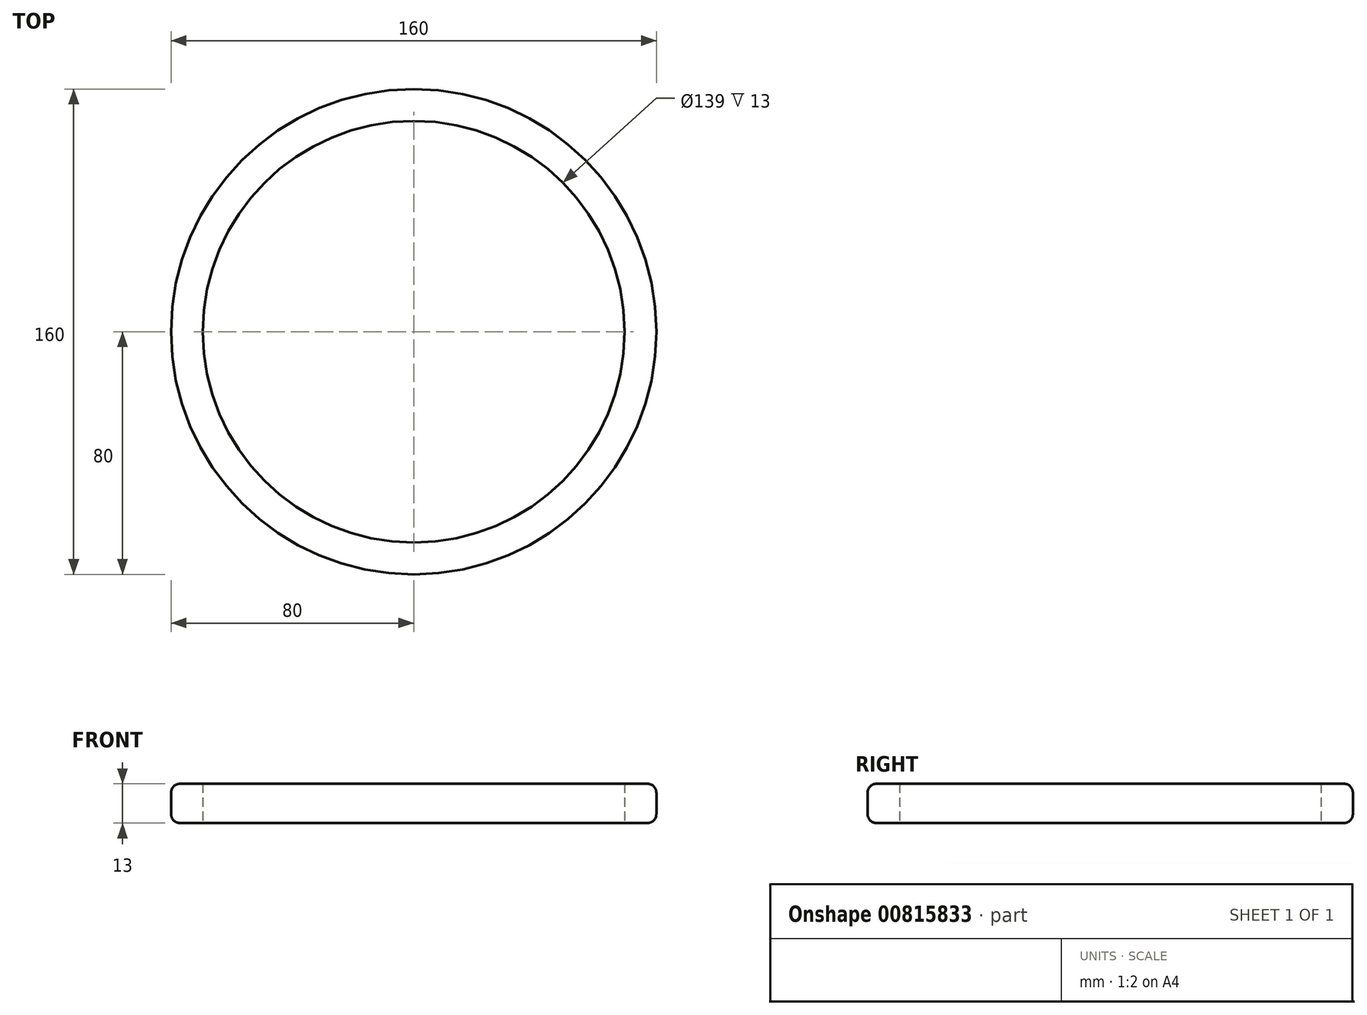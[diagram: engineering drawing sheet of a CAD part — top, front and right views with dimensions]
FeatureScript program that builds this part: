
annotation { "Feature Type Name" : "Feature", "Feature Type Description" : "" }
export const myFeature = defineFeature(function(context is Context, id is Id, definition is map)
    precondition{}
    {
        {
            var Q0;
            Q0=qCreatedBy(makeId("Top.planeOp"),FACE);
            var sketch = newSketch(context, id + "F0", { "sketchPlane" : qUnion([Q0])});
            skCircle(sketch, "E0", {"center": v(0, 0) * mm, "radius": 69.5 * mm});
            skCircle(sketch, "E1", {"center": v(0, 0) * mm, "radius": 80 * mm});
            skSolve(sketch);
        }
        {
            var Q0;
            Q0=qSketchRegion(id+"F0",true);
            extrude(context, id + "F1", {"entities" : qUnion([Q0]), "depth" : 13 * mm, "offsetDistance" : 25 * mm});
        }
        {
            var Q0;
            Q0=makeQuery(id+"F1.opExtrude","CAP_EDGE",EDGE,{"disambiguationData":[OSD([sQuery(id+"F0.wireOp",EDGE,"E1")])],"isStart":false});
            var Q1;
            Q1=makeQuery(id+"F1.opExtrude","CAP_EDGE",EDGE,{"disambiguationData":[OSD([sQuery(id+"F0.wireOp",EDGE,"E1")])],"isStart":true});
            fillet(context, id + "F2", {"entities" : qUnion([Q0, Q1]), "radius" : 3 * mm, "tangentPropagation" : true, "allowEdgeOverflow" : false});
        }
    });
